# Revit family: Midmark - Mobile Lift Table
name_source: partatom
category: Specialty Equipment
revit_build: Autodesk Revit 2017 (Build: 20190507_1515(x64)
units: mm (PartAtom-declared; Revit-internal decimal feet)

## family parameters
Always vertical = Yes
Cut with Voids When Loaded = No
OmniClass Number = 23.25.61.00
Part Type = Normal
Room Calculation Point = No
Round Connector Dimension = Use Diameter
Shared = No
Work Plane-Based = No

## types (4) — shared parameters
Base Depth = 2' - 1"
Base Material = Stainless Steel, Polished
Base Width = 4' - 6"
Battery Charger Material = Stainless Steel, Polished
Cleat Material = Stainless Steel, Polished
Depth = 1' - 10"
Frame Material = Steel, Paint Finish, Black, Matte
Height = 3' - 0"
Manufacturer = MIDMARK
Side Rail Material = Stainless Steel, Polished
Table Top Material = Stainless Steel, Polished
zero-valued in all types: Weight

## per-type parameters (varying)
| type | Cleats | Description | Frame Width | Model | No Cleats | No Scale | No Side Rails | Scale | Side Rails & Cleats | Type Comments | Width |
| Stainless Steel Top | No |  | 3' - 10" | 103-0170-16 | Yes | Yes | Yes | No | No | Mobile Lift Table, 50"L x 22"W Stainless Steel Top. | 4' - 2" |
| Stainless Steel Top with Scale | No | Cleats and Side Rails are Not Available on Table with Built-in Scale. | 3' - 4" | 110-3410-08 | Yes | No | Yes | Yes | No | Mobile Lift Table. 50"L x 22"W Stainless Steel Top with Built-in Scale. | 3' - 8" |
| Stainless Steel Top with Side Rails | No |  | 3' - 10" | 103-0170-16 & 203-0170-10 | Yes | Yes | No | No | Yes | Mobile Lift Table. 50"L x 22"W Stainless Steel Top with Side Rails | 4' - 2" |
| Stainless Steel Top with Cleats | Yes |  | 3' - 10" | 103-0170-16 & 203-0170-20 | No | Yes | Yes | No | No | Mobile Lift Table, 50"L x 22"W Stainless Steel Top with Quick-release Restraint Cleats. | 4' - 2" |

## geometry (parser evidence)
native form markers: Sweep x7
no freeform markers — native parametric forms only
